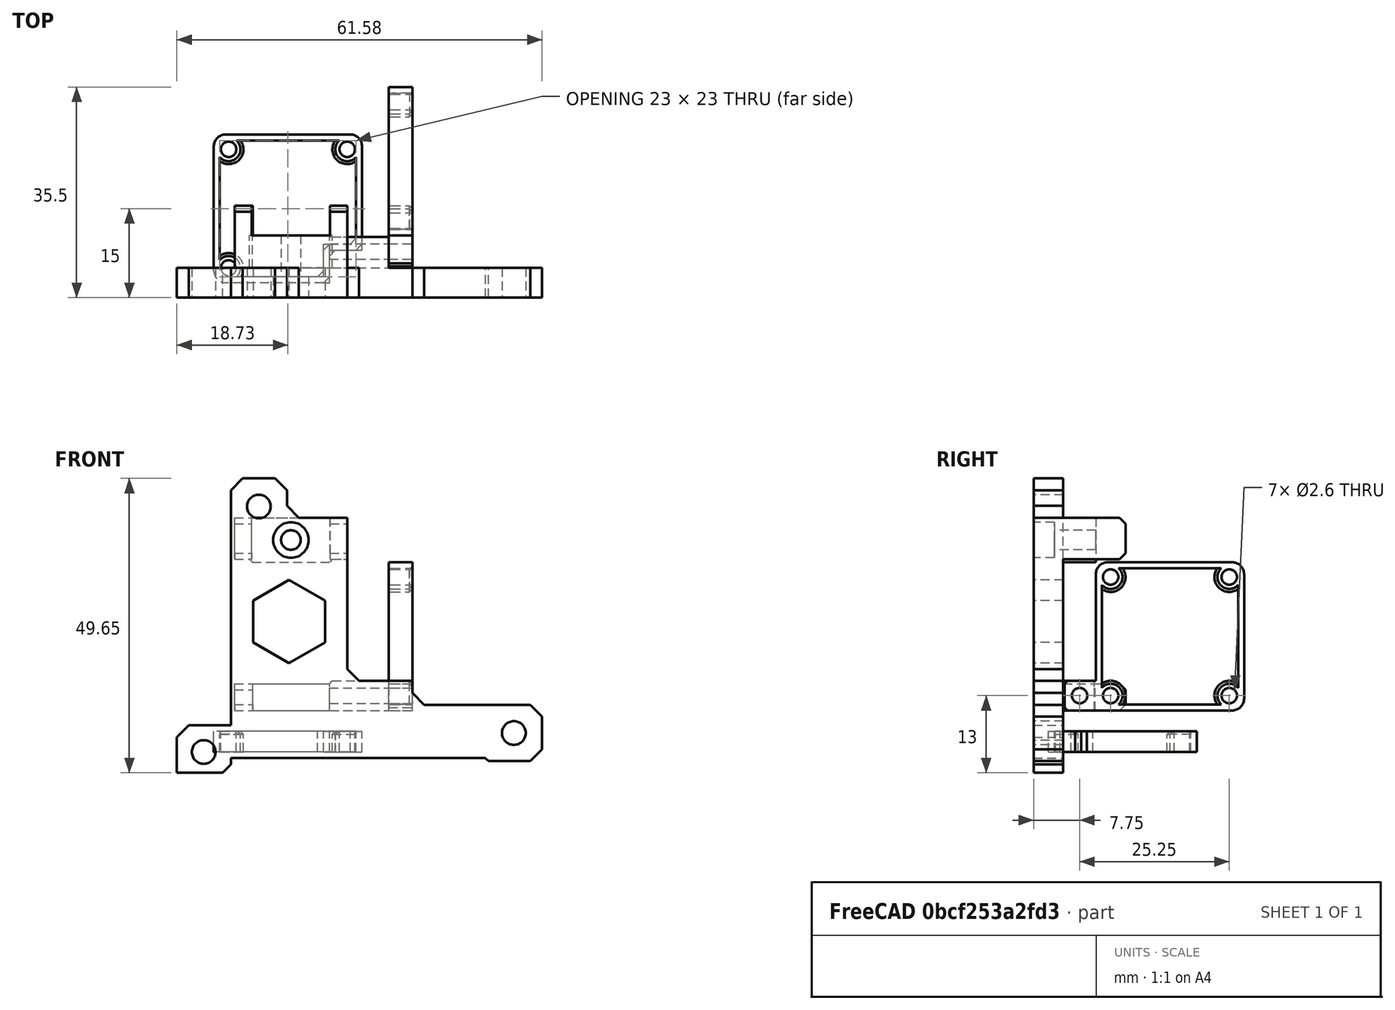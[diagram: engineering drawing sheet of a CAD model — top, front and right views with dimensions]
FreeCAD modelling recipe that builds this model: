
FCSTD DOCUMENT  (FreeCAD 0.18R16146 (Git))
Label: dual-fan-adapter
License: All rights reserved
LicenseURL: http://en.wikipedia.org/wiki/All_rights_reserved
objects: Part::Feature×6, Part::Box×6, Part::MultiFuse×5, Part::Chamfer×4, Part::Cut×4, Part::Cylinder×2
note: 27 computed .brp shape members not serialized (recipe doc carries the construction recipe); baked Part::Feature solids carry a one-line shape summary decoded from their .brp

FEATURE [Part::Feature] Cut036009013017007008008021005005006  label="dual-fan-adapter"
  Placement = pos=(-0.5,-5.5,-3e-15) rot=(0,-1,0;1.5708rad)
  shape: bbox 25 x 25 x 3.5 mm, 25 faces (baked)
FEATURE [Part::Box] Box  label="Cube"
  AttacherType = Attacher::AttachEngine3D
  Height = 3.5
  Length = 1
  Placement = pos=(5.5,-18,0) rot=(0,0,1;0rad)
  Width = 6.5
FEATURE [Part::Box] Box001  label="Cube001"
  AttacherType = Attacher::AttachEngine3D
  Height = 3.5
  Length = 6.5
  Placement = pos=(5.5,-12.5,0) rot=(0,0,1;0rad)
  Width = 1
FEATURE [Part::MultiFuse] Fusion
  Shapes = -> [Box001,Box,Cut036009013017007008008021005005006]
FEATURE [Part::Feature] Fusion001
  shape: bbox 25 x 25 x 3.5 mm, 27 faces (baked)
FEATURE [Part::Chamfer] Chamfer
  Base = -> Fusion001
  Edges = 3 edges r=1: [Edge84,Edge85,Edge86]
FEATURE [Part::Chamfer] Chamfer001  label="adapter-cutout"
  Base = -> Chamfer
  Edges = 3 edges r=1: [Edge62,Edge64,Edge86]
FEATURE [Part::Feature] Cut036009013017007008008021005005041  label="fan-mount-r002"
  Placement = pos=(0,35,0) rot=(0,0,1;0rad)
  shape: bbox 61.58 x 15.5 x 49.65 mm, 84 faces (baked)
FEATURE [Part::Feature] Cut036009013017007008008021005005042  label="dual-fan-adapter001"
  Placement = pos=(-0.5,-5.5,-3e-15) rot=(0,-1,0;1.5708rad)
  shape: bbox 25 x 25 x 3.5 mm, 25 faces (baked)
FEATURE [Part::Feature] Cut036009013017007008008021005005043  label="dual-fan-adapter002"
  Placement = pos=(-0.5,-5.5,-3e-15) rot=(0.57735,-0.57735,0.57735;2.0944rad)
  shape: bbox 25 x 25 x 3.5 mm, 25 faces (baked)
FEATURE [Part::MultiFuse] Fusion002
  Placement = pos=(16.5,8,19) rot=(0,1,0;1.5708rad)
  Shapes = -> [Cut036009013017007008008021005005043,Cut036009013017007008008021005005042]
FEATURE [Part::Feature] Fusion002001  label="Fusion003"
  Placement = pos=(17,8,19) rot=(0,1,0;1.5708rad)
  shape: bbox 3.5 x 25 x 25 mm, 44 faces (baked)
FEATURE [Part::MultiFuse] Fusion002002
  Shapes = -> [Fusion002001,Fusion002]
FEATURE [Part::Box] Box002  label="Cube002"
  AttacherType = Attacher::AttachEngine3D
  Height = 5
  Length = 4
  Placement = pos=(16.5,-15.25,7) rot=(0,0,1;0rad)
  Width = 8
FEATURE [Part::Box] Box003  label="Cube003"
  AttacherType = Attacher::AttachEngine3D
  Height = 5
  Length = 4
  Placement = pos=(16.5,-15.5,7) rot=(0,0,1;0rad)
  Width = 13
FEATURE [Part::Cut] Cut
  Base = -> Cut036009013017007008008021005005041
  Tool = -> Box003
FEATURE [Part::Box] Box004  label="Cube004"
  AttacherType = Attacher::AttachEngine3D
  Height = 5
  Length = 4
  Placement = pos=(16.5,-9,8) rot=(0,0,1;0rad)
  Width = 7
FEATURE [Part::Cut] Cut036009013017007008008021005005044
  Base = -> Box002
  Tool = -> Box004
FEATURE [Part::Cylinder] Cylinder
  Angle = 360
  AttacherType = Attacher::AttachEngine3D
  Height = 16
  Placement = pos=(6.5,-12.75,9.5) rot=(0,1,0;1.5708rad)
  Radius = 1.3
FEATURE [Part::Chamfer] Chamfer002
  Base = -> Cut036009013017007008008021005005044
  Edges = 2 edges r=0.5: [Edge9,Edge17]
FEATURE [Part::Box] Box005  label="Cube005"
  AttacherType = Attacher::AttachEngine3D
  Height = 1
  Length = 10
  Placement = pos=(6.5,-15.5,11) rot=(0,0,1;0rad)
  Width = 5.25
FEATURE [Part::Chamfer] Chamfer003
  Base = -> Box005
  Edges = 1 edges r=0.5: [Edge2]
FEATURE [Part::MultiFuse] Fusion002003
  Shapes = -> [Chamfer003,Cut]
FEATURE [Part::Cylinder] Cylinder001
  Angle = 360
  AttacherType = Attacher::AttachEngine3D
  Height = 16
  Placement = pos=(6.5,-12.75,9.5) rot=(0,1,0;1.5708rad)
  Radius = 1.3
FEATURE [Part::Cut] Cut036009013017007008008021005005046
  Base = -> Fusion002003
  Tool = -> Cylinder001
FEATURE [Part::Cut] Cut036009013017007008008021005005047
  Base = -> Chamfer002
  Tool = -> Cylinder
FEATURE [Part::MultiFuse] Fusion002004
  Shapes = -> [Fusion002002,Cut036009013017007008008021005005047]
